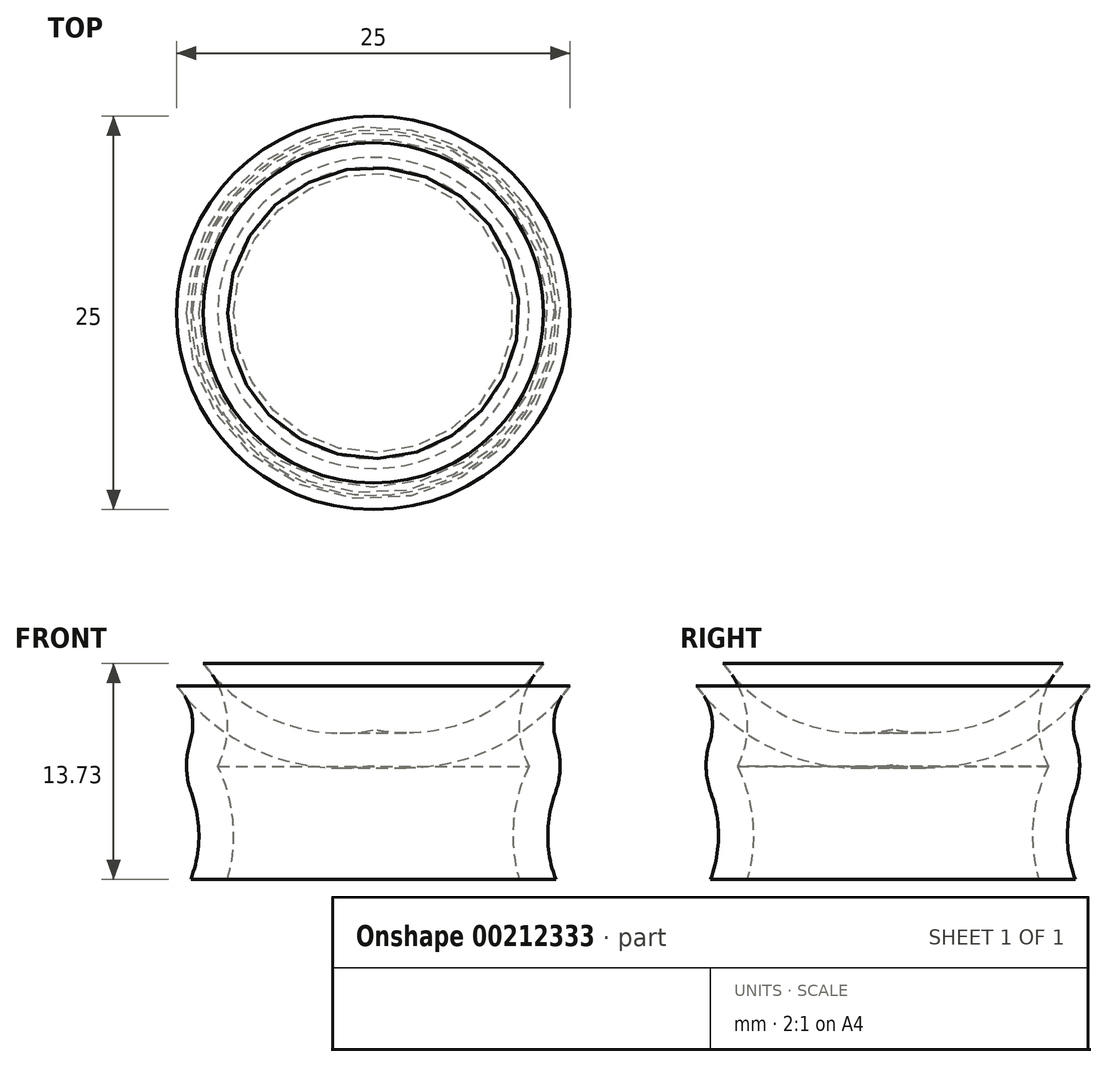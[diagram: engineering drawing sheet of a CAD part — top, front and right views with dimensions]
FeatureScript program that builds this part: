
annotation { "Feature Type Name" : "Feature", "Feature Type Description" : "" }
export const myFeature = defineFeature(function(context is Context, id is Id, definition is map)
    precondition{}
    {
        {
            var Q0;
            Q0=qCreatedBy(makeId("Front.planeOp"),FACE);
            var sketch = newSketch(context, id + "F0", { "sketchPlane" : qUnion([Q0])});
            skLineSegment(sketch, "E0", {"start": v(0, 0) * mm, "end": v(0, 41.3) * mm, "construction": true});
            skLineSegment(sketch, "E1", {"start": v(0, 27.3) * mm, "end": v(-15, 27.3) * mm, "construction": true});
            skLineSegment(sketch, "E2", {"start": v(0, 20.8) * mm, "end": v(-12.5, 20.8) * mm, "construction": true});
            skArc(sketch, "E3", {"start": v(0, 41.3) * mm, "mid": v(-13.17, 35.27) * mm, "end": v(-12.5, 20.8) * mm});
            skLineSegment(sketch, "E4", {"start": v(0, 18.8) * mm, "end": v(-11.5, 18.8) * mm, "construction": true});
            skLineSegment(sketch, "E5", {"start": v(0, 15.8) * mm, "end": v(-12.5, 15.8) * mm});
            skLineSegment(sketch, "E6", {"start": v(0, 12.8) * mm, "end": v(-11.23, 12.8) * mm, "construction": true});
            skArc(sketch, "E7", {"start": v(-11.63, 17.23) * mm, "mid": v(-11.56, 19.14) * mm, "end": v(-12.5, 20.8) * mm});
            skLineSegment(sketch, "E8", {"start": v(0, 8.5) * mm, "end": v(-11.6, 8.5) * mm, "construction": true});
            skArc(sketch, "E9", {"start": v(-11.6, 8.5) * mm, "mid": v(-11.08, 11.25) * mm, "end": v(-11.56, 14) * mm});
            skPoint(sketch, "E10.visualSharp", {"position": v(-12.5, 15.8) * mm});
            skArc(sketch, "E10.filletArc", {"start": v(-11.63, 17.23) * mm, "mid": v(-11.86, 15.6) * mm, "end": v(-11.56, 14) * mm});
            skArc(sketch, "E11.0", {"start": v(-9.26, 8.5) * mm, "mid": v(-8.9, 12.15) * mm, "end": v(-9.88, 15.7) * mm});
            skArc(sketch, "E11.1", {"start": v(-9.88, 15.7) * mm, "mid": v(-9.31, 19.1) * mm, "end": v(-10.8, 22.23) * mm});
            skArc(sketch, "E11.2", {"start": v(0, 39.05) * mm, "mid": v(-11.15, 34.33) * mm, "end": v(-10.8, 22.23) * mm});
            skLineSegment(sketch, "E12", {"start": v(0, 41.3) * mm, "end": v(0, 39.05) * mm});
            skLineSegment(sketch, "E13", {"start": v(-11.6, 8.5) * mm, "end": v(-9.26, 8.5) * mm});
            skSolve(sketch);
        }
        {
            var Q0;
            Q0=makeQuery(id+"F0.imprint","IMPRINT",FACE,{"disambiguationData":[TD([[makeQuery(id+"F0.imprint","IMPRINT",EDGE,{"derivedFrom":sQuery(id+"F0.wireOp",EDGE,"E3")}),1.0]])]});
            var Q1;
            {var subQ2=sQuery(id+"F0.wireOp",EDGE,"E9");Q1=makeQuery(id+"F0.imprint","IMPRINT",FACE,{"disambiguationData":[TD([[makeQuery(id+"F0.imprint","IMPRINT",EDGE,{"derivedFrom":subQ2}),-1.0]])]});}
            var Q2;
            Q2=sQuery(id+"F0.wireOp",EDGE,"E0");
            revolve(context, id + "F1", {"entities" : qUnion([Q0, Q1]), "axis" : qUnion([Q2]), "revolveType" : RevolveType.FULL});
        }
    });
